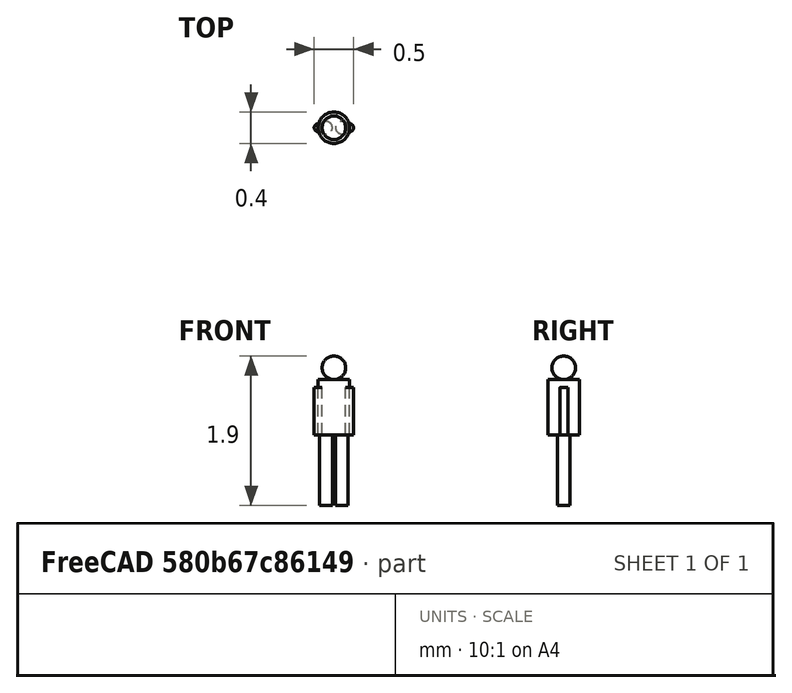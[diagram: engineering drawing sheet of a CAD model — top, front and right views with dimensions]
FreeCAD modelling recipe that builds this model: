
FCSTD DOCUMENT  (FreeCAD 0.18.4R)
Label: cylinder
License: All rights reserved
LicenseURL: http://en.wikipedia.org/wiki/All_rights_reserved
objects: Part::Cylinder×5, Part::Sphere×1
note: 6 computed .brp shape members not serialized (recipe doc carries the construction recipe); baked Part::Feature solids carry a one-line shape summary decoded from their .brp

FEATURE [Part::Cylinder] Cylinder  label="trunk"
  Angle = 360
  AttacherType = Attacher::AttachEngine3D
  Height = 0.7
  Placement = pos=(0,0,0.9) rot=(0,0,1;0rad)
  Radius = 0.2
FEATURE [Part::Sphere] Sphere  label="head"
  Angle1 = -90
  Angle2 = 90
  Angle3 = 360
  AttacherType = Attacher::AttachEngine3D
  Placement = pos=(0,0,1.75) rot=(0,0,1;0rad)
  Radius = 0.15
FEATURE [Part::Cylinder] Cylinder001  label="left arm"
  Angle = 360
  AttacherType = Attacher::AttachEngine3D
  Height = 0.6
  Placement = pos=(-0.2,0,0.9) rot=(0,0,1;0rad)
  Radius = 0.05
FEATURE [Part::Cylinder] Cylinder002  label="right arm"
  Angle = 360
  AttacherType = Attacher::AttachEngine3D
  Height = 0.6
  Placement = pos=(0.2,0,0.9) rot=(0,0,1;0rad)
  Radius = 0.05
FEATURE [Part::Cylinder] Cylinder003  label="left leg"
  Angle = 360
  AttacherType = Attacher::AttachEngine3D
  Height = 0.9
  Placement = pos=(-0.1,0,0) rot=(0,0,1;0rad)
  Radius = 0.08
FEATURE [Part::Cylinder] Cylinder004  label="right leg"
  Angle = 360
  AttacherType = Attacher::AttachEngine3D
  Height = 0.9
  Placement = pos=(0.1,0,0) rot=(0,0,1;0rad)
  Radius = 0.08
